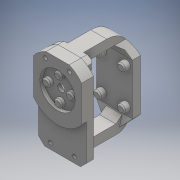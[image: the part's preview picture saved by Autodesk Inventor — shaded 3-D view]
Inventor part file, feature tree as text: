
AUTODESK INVENTOR PART (.ipt)
format: ipt  version: 2016 (Build 200138000, 138)  size: 459,264 bytes
history: native  units: mm
features: sketch x16, extrude x14, chamfer x9, projected_geometry x9, hole x3, fillet x2
ambient origin geometry x8: Origin, YZ Plane, XZ Plane, XY Plane, X Axis, Y Axis, Z Axis, Center Point
bodies: Solid1 (feature_tree), Solid2 (feature_tree)
feature tree (53):
  extrude  "Extrusion1"  Depth=2.0mm TaperAngle=0.0deg
  extrude  "Extrusion2"  Depth=2.5mm TaperAngle=0.0deg
  extrude  "Extrusion3"  Depth=6.0mm
  chamfer  "Chamfer1"  Distance=40.0mm Angle=360.0deg
  extrude  "Extrusion4"  Depth=0.6mm TaperAngle=45.0deg
  extrude  "Extrusion5"  Depth=18.0mm
  chamfer  "Chamfer2"  Distance=1.5mm
  extrude  "Extrusion6"  Depth=6.0mm
  hole  "Hole1"  [1 undecoded]
  chamfer  "Chamfer3"  Distance=3.0mm
  extrude  "Extrusion7"  Depth=3.0mm TaperAngle=0.0deg
  extrude  "Extrusion8"  Depth=12.0mm
  chamfer  "Chamfer5"  Distance=3.0mm Angle=45.0deg
  extrude  "Extrusion9"  Depth=3.0mm TaperAngle=0.0deg
  extrude  "Extrusion10"  Depth=18.0mm TaperAngle=0.0deg
  extrude  "Extrusion11"  Depth=0.6mm TaperAngle=45.0deg
  chamfer  "Chamfer7"  Distance=6.0mm
  chamfer  "Chamfer8"  Distance=1.5mm
  chamfer  "Chamfer9"  Distance=1.5mm
  extrude  "Extrusion12"  Depth=1.5mm TaperAngle=45.0deg
  chamfer  "Chamfer10"  Distance=1.5mm Angle=45.0deg
  fillet  "Fillet1"  Radius=0.6mm
  fillet  "Fillet2"  Radius=4.0mm
  hole  "Hole2"  [1 undecoded]
  extrude  "Extrusion13"  Depth=0.6mm
  chamfer  "Chamfer11"  Distance=1.5mm
  hole  "Hole3"  [1 undecoded]
  extrude  "Extrusion14"  Depth=12.0mm
  sketch  "Sketch1"  dims[d0=30.0mm d1=2.0mm d2=0.0mm]
  sketch  "Sketch2"  dims[d3=17.65mm d4=2.5mm d5=0.0mm]
  sketch  "Sketch3"  dims[d6=3.95mm d7=6.0mm d8=40.0mm d10=360.0deg]
  sketch  "Sketch4"  dims[d12=2.5mm d13=0.0mm d14=0.6mm d15=2.0mm d16=45.0deg]
  sketch  "Sketch5"  dims[d17=30.0mm d18=18.0mm]
  sketch  "Sketch6"  dims[d19=25.5mm]
  sketch  "Sketch7"  dims[d21=3.25mm d22=1.5mm d23=0.0mm]
  sketch  "Sketch8"  dims[d24=3.95mm d25=6.0mm]
  sketch  "Sketch9"  dims[d26=3.25mm d27=20.0mm d29=12.0mm d30=20.0mm d32=18.0mm d35=3.0mm d36=0.0mm]
  sketch  "Sketch10"  dims[d37=0.6mm d38=2.0mm d39=45.0deg d40=3.0mm d41=0.0mm]
  projected_geometry  "Projected Loop2"
  projected_geometry  "Projected Loop3"
  sketch  "Sketch11"  dims[d42=12.0mm d45=11.0mm]
  projected_geometry  "Projected Loop4"
  sketch  "Sketch12"  dims[d47=12.0mm]
  projected_geometry  "Projected Loop5"
  projected_geometry  "Projected Loop6"
  projected_geometry  "Projected Loop7"
  sketch  "Sketch13"  dims[d49=27.0mm]
  sketch  "Sketch14"  dims[d50=1.9mm d51=6.0mm d52=4.0mm d53=2.0mm d54=90.0deg d55=8.0mm d56=20.594885mm d57=3.0mm d58=2.0mm d59=45.0deg]
  projected_geometry  "Projected Loop8"
  projected_geometry  "Projected Loop9"
  sketch  "Sketch15"  dims[d60=9.1mm d61=3.0mm d62=0.0mm]
  sketch  "Sketch16"  dims[d63=3.0mm d64=18.0mm d65=0.0mm d69=1.985942mm d70=2.0mm d71=45.0deg d75=6.0mm d76=0.0mm d77=1.5mm d78=0.0mm d79=1.5mm d80=0.0mm d81=5.3mm d82=1.5mm d83=45.0deg d84=5.85mm d85=1.5mm d86=45.0deg d87=0.6mm d88=1.5mm d89=45.0deg d90=4.0mm d91=4.0mm d92=4.0mm d93=1.5mm d94=0.0mm d95=2.5mm d96=1.5mm d97=45.0deg d98=12.0mm d99=6.0mm d100=2.1mm d101=6.0mm d102=4.0mm d103=24.5mm d104=90.0deg d105=8.0mm d106=20.594885mm d107=6.0mm d108=3.0mm d109=1.5mm d110=0.0mm d111=1.0mm d112=1.5mm d113=45.0deg d114=10.0mm d115=10.0mm d116=3.5mm d117=6.0mm d118=6.0mm d119=1.0mm d120=90.0deg d121=8.0mm d122=20.594885mm d123=0.6mm d124=0.0mm]
  projected_geometry  "Projected Loop10"
note: 3 required parameter values undecoded (feature->parameter linkage not recoverable at this tier; creation-order binding heuristic only, values carry confidence <= 0.55)
